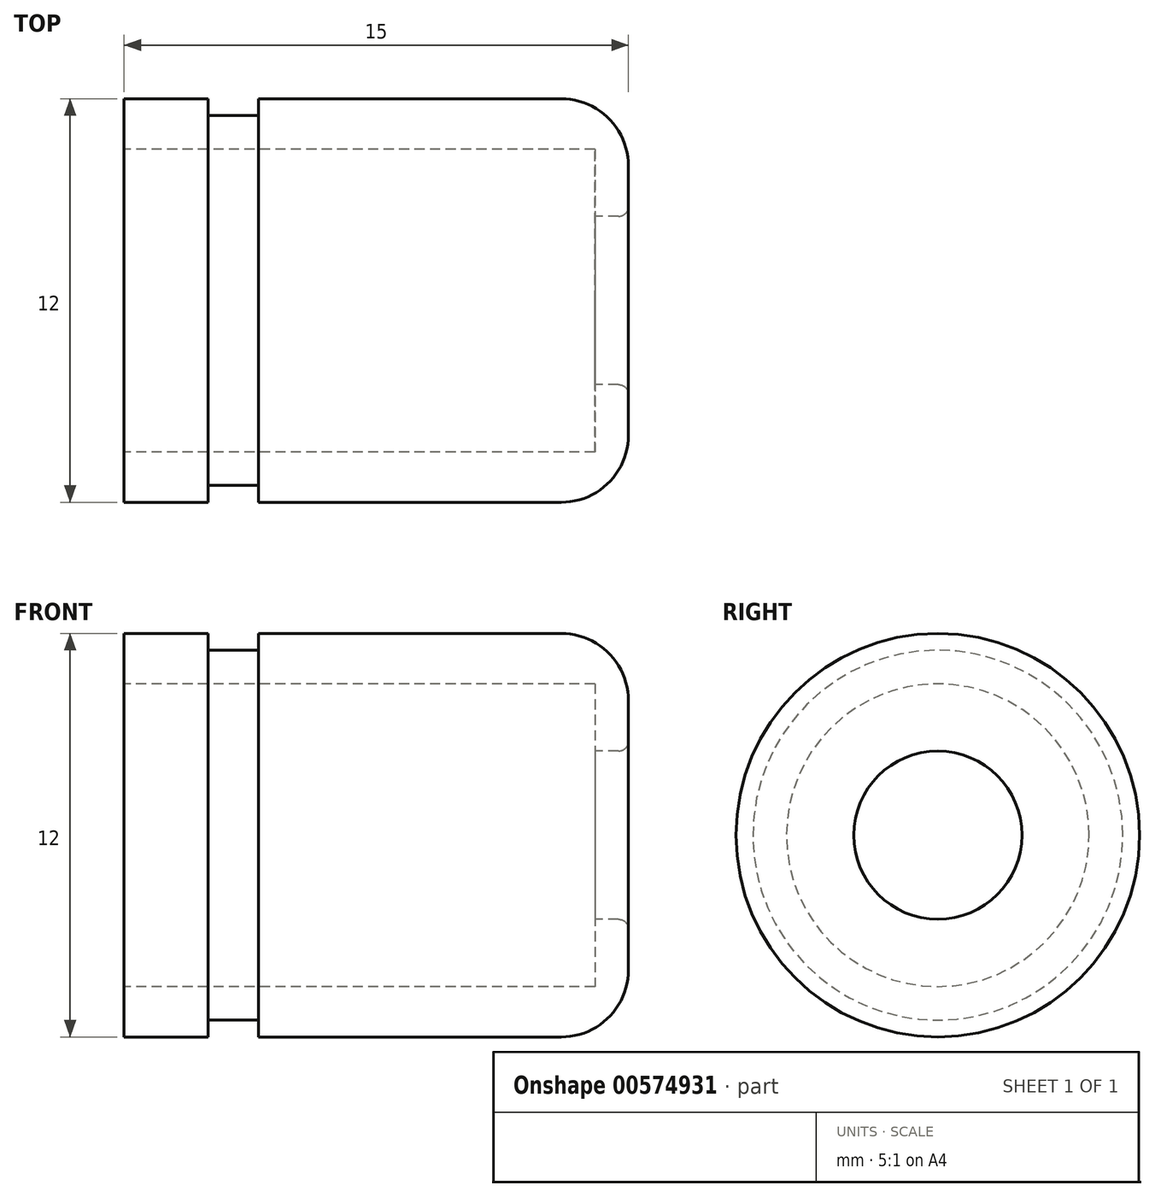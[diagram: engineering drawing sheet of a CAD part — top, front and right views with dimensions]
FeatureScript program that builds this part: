
annotation { "Feature Type Name" : "Feature", "Feature Type Description" : "" }
export const myFeature = defineFeature(function(context is Context, id is Id, definition is map)
    precondition{}
    {
        {
            var Q0;
            Q0=qCreatedBy(makeId("Front.planeOp"),FACE);
            var sketch = newSketch(context, id + "F0", { "sketchPlane" : qUnion([Q0])});
            skLineSegment(sketch, "E0", {"start": v(0, 4.5) * mm, "end": v(0, 6) * mm});
            skLineSegment(sketch, "E1", {"start": v(0, 6) * mm, "end": v(2.5, 6) * mm});
            skLineSegment(sketch, "E2", {"start": v(2.5, 6) * mm, "end": v(2.5, 5.5) * mm});
            skLineSegment(sketch, "E3", {"start": v(2.5, 5.5) * mm, "end": v(4, 5.5) * mm});
            skLineSegment(sketch, "E4", {"start": v(4, 5.5) * mm, "end": v(4, 6) * mm});
            skLineSegment(sketch, "E5", {"start": v(4, 6) * mm, "end": v(13, 6) * mm});
            skLineSegment(sketch, "E6", {"start": v(15, 4) * mm, "end": v(15, 2.8) * mm});
            skLineSegment(sketch, "E7", {"start": v(14.7, 2.5) * mm, "end": v(14, 2.5) * mm});
            skLineSegment(sketch, "E8", {"start": v(14, 2.5) * mm, "end": v(14, 4.5) * mm});
            skLineSegment(sketch, "E9", {"start": v(14, 4.5) * mm, "end": v(0, 4.5) * mm});
            skPoint(sketch, "E10.visualSharp", {"position": v(15, 6) * mm});
            skArc(sketch, "E10.filletArc", {"start": v(15, 4) * mm, "mid": v(14.41, 5.41) * mm, "end": v(13, 6) * mm});
            skPoint(sketch, "E11.visualSharp", {"position": v(4, 6) * mm});
            skLineSegment(sketch, "E11.filletArc", {"start": v(4, 6) * mm, "end": v(4, 6) * mm});
            skPoint(sketch, "E12.visualSharp", {"position": v(2.5, 6) * mm});
            skLineSegment(sketch, "E12.filletArc", {"start": v(2.5, 6) * mm, "end": v(2.5, 6) * mm});
            skPoint(sketch, "E13.visualSharp", {"position": v(15, 2.5) * mm});
            skLineSegment(sketch, "E13.filletArc", {"start": v(15, 2.5) * mm, "end": v(15, 2.5) * mm});
            skPoint(sketch, "E14.visualSharp", {"position": v(14, 2.5) * mm});
            skLineSegment(sketch, "E14.filletArc", {"start": v(14, 2.5) * mm, "end": v(14, 2.5) * mm});
            skLineSegment(sketch, "E15", {"start": v(0, 0) * mm, "end": v(17, 0) * mm, "construction": true});
            skArc(sketch, "E16.filletArc", {"start": v(14.7, 2.5) * mm, "mid": v(14.91, 2.59) * mm, "end": v(15, 2.8) * mm});
            skSolve(sketch);
        }
        {
            var Q0;
            Q0 = qSketchRegion(id + "F0", true);
            var Q1;
            Q1=sQuery(id+"F0.wireOp",EDGE,"E15");
            revolve(context, id + "F1", {"entities" : qUnion([Q0]), "axis" : qUnion([Q1]), "revolveType" : RevolveType.FULL});
        }
    });
